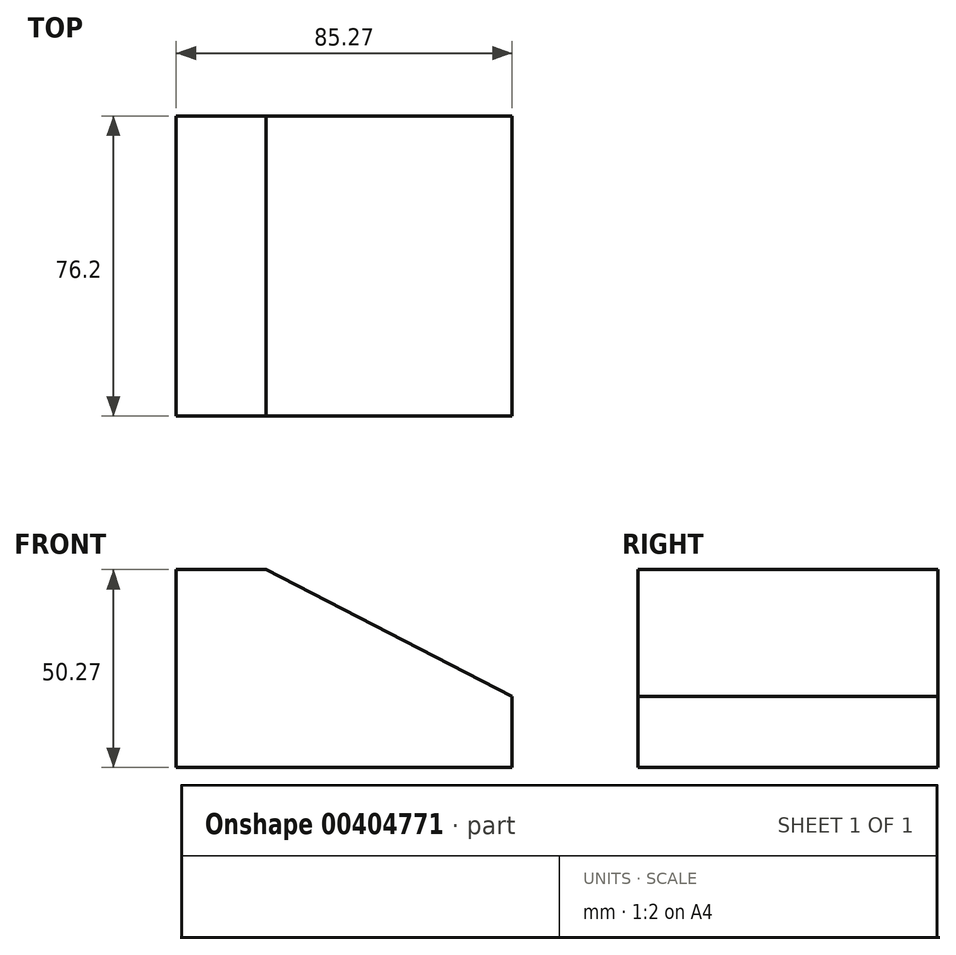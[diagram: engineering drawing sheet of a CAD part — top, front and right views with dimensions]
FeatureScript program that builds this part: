
annotation { "Feature Type Name" : "Feature", "Feature Type Description" : "" }
export const myFeature = defineFeature(function(context is Context, id is Id, definition is map)
    precondition{}
    {
        {
            var Q0;
            Q0=qCreatedBy(makeId("Front.planeOp"),FACE);
            var sketch = newSketch(context, id + "F0", { "sketchPlane" : qUnion([Q0])});
            skLineSegment(sketch, "E0.bottom", {"start": v(-107.7, 20.44) * mm, "end": v(-84.88, 20.44) * mm});
            skLineSegment(sketch, "E0.top", {"start": v(-107.7, -29.83) * mm, "end": v(-22.43, -29.83) * mm});
            skLineSegment(sketch, "E0.left", {"start": v(-107.7, 20.44) * mm, "end": v(-107.7, -29.83) * mm});
            skLineSegment(sketch, "E1", {"start": v(-84.88, 20.44) * mm, "end": v(-22.43, -11.81) * mm});
            skLineSegment(sketch, "E2.trimOffspring", {"start": v(-22.43, -11.81) * mm, "end": v(-22.43, -29.83) * mm});
            skSolve(sketch);
        }
        {
            var Q0;
            Q0=makeQuery(id+"F0.imprint","IMPRINT",FACE,{"disambiguationData":[TD([[makeQuery(id+"F0.imprint","IMPRINT",EDGE,{"derivedFrom":sQuery(id+"F0.wireOp",EDGE,"E0.bottom")}),-1.0]])]});
            extrude(context, id + "F1", {"entities" : qUnion([Q0]), "depth" : 76.2 * mm});
        }
    });
